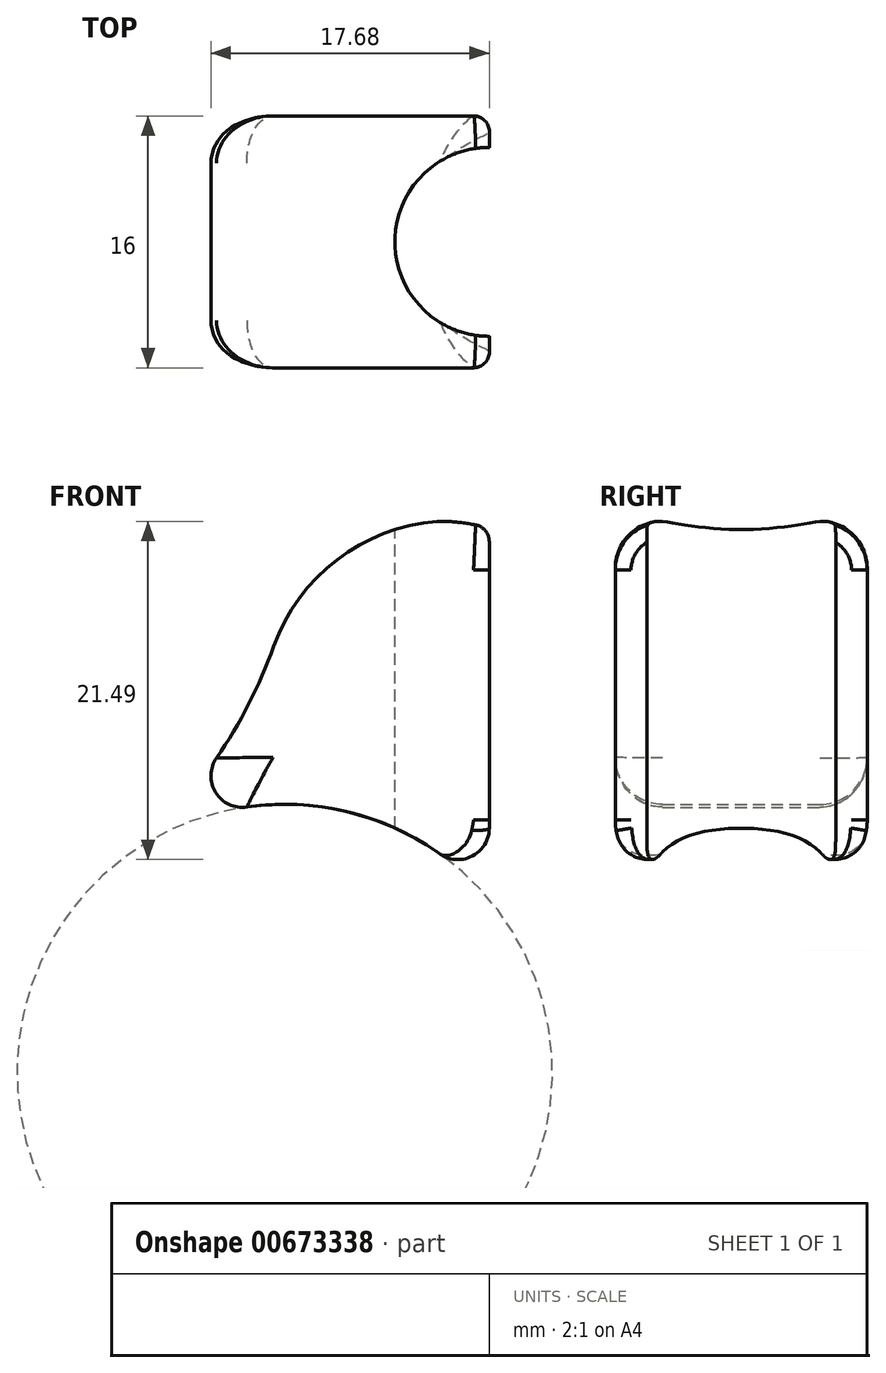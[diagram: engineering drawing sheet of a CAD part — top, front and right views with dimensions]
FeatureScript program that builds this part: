
annotation { "Feature Type Name" : "Feature", "Feature Type Description" : "" }
export const myFeature = defineFeature(function(context is Context, id is Id, definition is map)
    precondition{}
    {
        {
            var Q0;
            Q0=qCreatedBy(makeId("Front.planeOp"),FACE);
            var sketch = newSketch(context, id + "F0", { "sketchPlane" : qUnion([Q0])});
            skCircle(sketch, "E0", {"center": v(0, 0) * mm, "radius": 9 * mm});
            skCircle(sketch, "E1", {"center": v(0, 4) * mm, "radius": 17 * mm});
            skLineSegment(sketch, "E2", {"start": v(0, 9) * mm, "end": v(13, 9) * mm});
            skLineSegment(sketch, "E3", {"start": v(13, 9) * mm, "end": v(13, 39) * mm});
            skLineSegment(sketch, "E4", {"start": v(13, 39) * mm, "end": v(1, 39) * mm});
            skArc(sketch, "E5", {"start": v(-10.97, 16.99) * mm, "mid": v(-2.63, 26.71) * mm, "end": v(1, 39) * mm});
            skLineSegment(sketch, "E6", {"start": v(0, 0) * mm, "end": v(-3.12, -12.71) * mm});
            skSolve(sketch);
        }
        {
            var Q0;
            {var subQ0=sQuery(id+"F0.wireOp",EDGE,"E2");Q0=makeQuery(id+"F0.imprint","IMPRINT",FACE,{"disambiguationData":[TD([[makeQuery(id+"F0.imprint","IMPRINT",EDGE,{"derivedFrom":subQ0}),1.0]])]});}
            var Q1;
            {var subQ5=sQuery(id+"F0.wireOp",EDGE,"E4");Q1=makeQuery(id+"F0.imprint","IMPRINT",FACE,{"disambiguationData":[TD([[makeQuery(id+"F0.imprint","IMPRINT",EDGE,{"derivedFrom":subQ5}),1.0]])]});}
            extrude(context, id + "F1", {"entities" : qUnion([Q0, Q1]), "depth" : 16 * mm, "offsetDistance" : 25 * mm});
        }
        {
            var Q0;
            Q0=makeQuery(id+"F1.opExtrude","SWEPT_FACE",FACE,{"disambiguationData":[OSD([sQuery(id+"F0.wireOp",EDGE,"E4")])]});
            var sketch = newSketch(context, id + "F2", { "sketchPlane" : qUnion([Q0])});
            skCircle(sketch, "E7", {"center": v(13, -8) * mm, "radius": 6 * mm});
            skSolve(sketch);
        }
        {
            var Q0;
            {var subQ0=sQuery(id+"F2.wireOp",EDGE,"E7");var subQ1=makeQuery(id+"F1.opExtrude","SWEPT_EDGE",EDGE,{"disambiguationData":[OSD([sQuery(id+"F0.wireOp",EDGE,"E3"),sQuery(id+"F0.wireOp",EDGE,"E4")])]});var subQ2=makeQuery(id+"F2.imprint","INTERSECT",VERTEX,{"disambiguationData":[OD(0.0)],"derivedFrom":[subQ1,subQ0]});Q0=makeQuery(id+"F2.imprint","IMPRINT",FACE,{"disambiguationData":[TD([[makeQuery(id+"F2.imprint","IMPRINT",EDGE,{"disambiguationData":[TD([[subQ2,-1.0]])],"derivedFrom":subQ0}),1.0]])]});}
            extrude(context, id + "F3", {"entities" : qUnion([Q0]), "operationType" : NewBodyOperationType.REMOVE, "endBound" : BoundingType.THROUGH_ALL, "oppositeDirection" : true, "depth" : 25 * mm, "offsetDistance" : 25 * mm});
        }
        {
            var Q0;
            Q0=makeQuery(id+"F1.opExtrude","SWEPT_FACE",FACE,{"disambiguationData":[OSD([sQuery(id+"F0.wireOp",EDGE,"E4")])]});
            var sketch = newSketch(context, id + "F4", { "sketchPlane" : qUnion([Q0])});
            skCircle(sketch, "E8", {"center": v(13, -8) * mm, "radius": 8 * mm});
            skCircle(sketch, "E9", {"center": v(13, -8) * mm, "radius": 11 * mm});
            skSolve(sketch);
        }
        {
            var Q0;
            {var subQ3=sQuery(id+"F0.wireOp",EDGE,"E4");var subQ12=makeQuery(id+"F1.opExtrude","CAP_EDGE",EDGE,{"disambiguationData":[OSD([subQ3])],"isStart":true});var subQ16=sQuery(id+"F4.wireOp",EDGE,"E9");var subQ17=makeQuery(id+"F4.imprint","INTERSECT",VERTEX,{"derivedFrom":[subQ12,subQ16]});Q0=makeQuery(id+"F4.imprint","IMPRINT",FACE,{"disambiguationData":[TD([[makeQuery(id+"F4.imprint","IMPRINT",EDGE,{"disambiguationData":[TD([[subQ17,-1.0]])],"derivedFrom":subQ16}),1.0]])]});}
            extrude(context, id + "F5", {"entities" : qUnion([Q0]), "depth" : 4 * mm, "offsetDistance" : 25 * mm});
        }
        {
            var Q0;
            Q0=makeQuery(id+"F5.opExtrude","SWEPT_BODY",BODY,{"disambiguationData":[OSD([sQuery(id+"F0.wireOp",EDGE,"E4"),sQuery(id+"F4.wireOp",EDGE,"E8"),sQuery(id+"F4.wireOp",EDGE,"E9")])]});
            transform(context, id + "F6", {"entities" : qUnion([Q0]), "transformType" : TransformType.TRANSLATION_3D, "dx" : 0 * mm, "dy" : 0 * mm, "dz" : -26 * mm, "makeCopy" : false});
        }
        {
            var Q0;
            Q0=makeQuery(id+"F5.opExtrude","SWEPT_BODY",BODY,{"disambiguationData":[OSD([sQuery(id+"F0.wireOp",EDGE,"E4"),sQuery(id+"F4.wireOp",EDGE,"E8"),sQuery(id+"F4.wireOp",EDGE,"E9")])]});
            var Q1;
            Q1=makeQuery(id+"F1.opExtrude","SWEPT_BODY",BODY,{"disambiguationData":[OSD([sQuery(id+"F0.wireOp",EDGE,"E0"),sQuery(id+"F0.wireOp",EDGE,"E1"),sQuery(id+"F0.wireOp",EDGE,"E2"),sQuery(id+"F0.wireOp",EDGE,"E3"),sQuery(id+"F0.wireOp",EDGE,"E4"),sQuery(id+"F0.wireOp",EDGE,"E5"),sQuery(id+"F0.wireOp",EDGE,"E6")])]});
            booleanBodies(context, id + "F7", {"operationType" : BooleanOperationType.SUBTRACTION, "tools" : qUnion([Q0]), "targets" : qUnion([Q1])});
        }
        {
            var Q0;
            Q0=makeQuery(id+"F1.opExtrude","SWEPT_EDGE",EDGE,{"disambiguationData":[OSD([sQuery(id+"F0.wireOp",EDGE,"E4"),sQuery(id+"F0.wireOp",EDGE,"E5")])]});
            fillet(context, id + "F8", {"entities" : qUnion([Q0]), "radius" : 12 * mm, "tangentPropagation" : true, "allowEdgeOverflow" : false});
        }
        {
            var Q0;
            Q0=makeQuery(id+"F1.opExtrude","SWEPT_EDGE",EDGE,{"disambiguationData":[OSD([sQuery(id+"F0.wireOp",EDGE,"E0"),sQuery(id+"F0.wireOp",EDGE,"E6")])]});
            var Q1;
            Q1=makeQuery(id+"F1.opExtrude","SWEPT_EDGE",EDGE,{"disambiguationData":[OSD([sQuery(id+"F0.wireOp",EDGE,"E1"),sQuery(id+"F0.wireOp",EDGE,"E6")])]});
            fillet(context, id + "F9", {"entities" : qUnion([Q0, Q1]), "radius" : 2 * mm, "tangentPropagation" : true, "allowEdgeOverflow" : false});
        }
        {
            var Q0;
            Q0=makeQuery(id+"F1.opExtrude","CAP_EDGE",EDGE,{"disambiguationData":[OSD([sQuery(id+"F0.wireOp",EDGE,"E1")])],"isStart":false});
            var Q1;
            Q1=makeQuery(id+"F1.opExtrude","CAP_EDGE",EDGE,{"disambiguationData":[OSD([sQuery(id+"F0.wireOp",EDGE,"E5")])],"isStart":true});
            var Q2;
            Q2=makeQuery(id+"F1.opExtrude","CAP_EDGE",EDGE,{"disambiguationData":[OSD([sQuery(id+"F0.wireOp",EDGE,"E1")])],"isStart":true});
            var Q3;
            {var subQ0=sQuery(id+"F0.wireOp",EDGE,"E5");var subQ1=sQuery(id+"F0.wireOp",EDGE,"E4");Q3=makeQuery(id+"F8.opFillet","BLEND_EDGE",EDGE,{"blendedFrom":[makeQuery(id+"F1.opExtrude","SWEPT_EDGE",EDGE,{"disambiguationData":[OSD([subQ1,subQ0])]}),makeQuery(id+"F1.opExtrude","CAP_FACE",FACE,{"disambiguationData":[OSD([sQuery(id+"F0.wireOp",EDGE,"E0"),sQuery(id+"F0.wireOp",EDGE,"E1"),sQuery(id+"F0.wireOp",EDGE,"E2"),sQuery(id+"F0.wireOp",EDGE,"E3"),subQ1,subQ0,sQuery(id+"F0.wireOp",EDGE,"E6")])],"isStart":false})],"blendedInto":[makeQuery(id+"F1.opExtrude","CAP_FACE",FACE,{"disambiguationData":[OSD([sQuery(id+"F0.wireOp",EDGE,"E0"),sQuery(id+"F0.wireOp",EDGE,"E1"),sQuery(id+"F0.wireOp",EDGE,"E2"),sQuery(id+"F0.wireOp",EDGE,"E3"),subQ1,subQ0,sQuery(id+"F0.wireOp",EDGE,"E6")])],"isStart":false})]});}
            var Q4;
            {var subQ0=sQuery(id+"F0.wireOp",EDGE,"E5");var subQ1=sQuery(id+"F0.wireOp",EDGE,"E4");Q4=makeQuery(id+"F8.opFillet","BLEND_EDGE",EDGE,{"blendedFrom":[makeQuery(id+"F1.opExtrude","SWEPT_EDGE",EDGE,{"disambiguationData":[OSD([subQ1,subQ0])]}),makeQuery(id+"F1.opExtrude","CAP_FACE",FACE,{"disambiguationData":[OSD([sQuery(id+"F0.wireOp",EDGE,"E0"),sQuery(id+"F0.wireOp",EDGE,"E1"),sQuery(id+"F0.wireOp",EDGE,"E2"),sQuery(id+"F0.wireOp",EDGE,"E3"),subQ1,subQ0,sQuery(id+"F0.wireOp",EDGE,"E6")])],"isStart":true})],"blendedInto":[makeQuery(id+"F1.opExtrude","CAP_FACE",FACE,{"disambiguationData":[OSD([sQuery(id+"F0.wireOp",EDGE,"E0"),sQuery(id+"F0.wireOp",EDGE,"E1"),sQuery(id+"F0.wireOp",EDGE,"E2"),sQuery(id+"F0.wireOp",EDGE,"E3"),subQ1,subQ0,sQuery(id+"F0.wireOp",EDGE,"E6")])],"isStart":true})]});}
            fillet(context, id + "F10", {"entities" : qUnion([Q0, Q1, Q2, Q3, Q4]), "radius" : 3 * mm, "allowEdgeOverflow" : false});
        }
        {
            var Q0;
            {var subQ0=sQuery(id+"F0.wireOp",EDGE,"E4");var subQ2=sQuery(id+"F0.wireOp",EDGE,"E3");Q0=makeQuery(id+"F7.opBoolean","SPLIT",EDGE,{"disambiguationData":[TD([makeQuery(id+"F1.opExtrude","SWEPT_FACE",FACE,{"disambiguationData":[OSD([subQ0])]})])],"derivedFrom":makeQuery(id+"F1.opExtrude","CAP_EDGE",EDGE,{"disambiguationData":[OSD([subQ2])],"isStart":false})});}
            var Q1;
            {var subQ1=sQuery(id+"F0.wireOp",EDGE,"E4");var subQ2=sQuery(id+"F0.wireOp",EDGE,"E3");Q1=makeQuery(id+"F7.opBoolean","SPLIT",EDGE,{"disambiguationData":[TD([makeQuery(id+"F1.opExtrude","SWEPT_FACE",FACE,{"disambiguationData":[OSD([subQ1])]})])],"derivedFrom":makeQuery(id+"F1.opExtrude","CAP_EDGE",EDGE,{"disambiguationData":[OSD([subQ2])],"isStart":true})});}
            var Q2;
            {var subQ0=sQuery(id+"F4.wireOp",EDGE,"E9");var subQ1=sQuery(id+"F0.wireOp",EDGE,"E4");Q2=makeQuery(id+"F7.opBoolean","COPY",EDGE,{"derivedFrom":makeQuery(id+"F5.opExtrude","SWEPT_EDGE",EDGE,{"disambiguationData":[OSD([subQ1,subQ0]),TDD([makeQuery(id+"F4.imprint","INTERSECT",VERTEX,{"derivedFrom":[makeQuery(id+"F1.opExtrude","CAP_EDGE",EDGE,{"disambiguationData":[OSD([subQ1])],"isStart":false}),subQ0]})])]})});}
            var Q3;
            {var subQ0=sQuery(id+"F4.wireOp",EDGE,"E9");var subQ1=sQuery(id+"F0.wireOp",EDGE,"E4");Q3=makeQuery(id+"F7.opBoolean","COPY",EDGE,{"derivedFrom":makeQuery(id+"F5.opExtrude","SWEPT_EDGE",EDGE,{"disambiguationData":[OSD([subQ1,subQ0]),TDD([makeQuery(id+"F4.imprint","INTERSECT",VERTEX,{"derivedFrom":[makeQuery(id+"F1.opExtrude","CAP_EDGE",EDGE,{"disambiguationData":[OSD([subQ1])],"isStart":true}),subQ0]})])]})});}
            fillet(context, id + "F11", {"entities" : qUnion([Q0, Q1, Q2, Q3]), "radius" : 1 * mm, "tangentPropagation" : true, "allowEdgeOverflow" : false});
        }
    });
